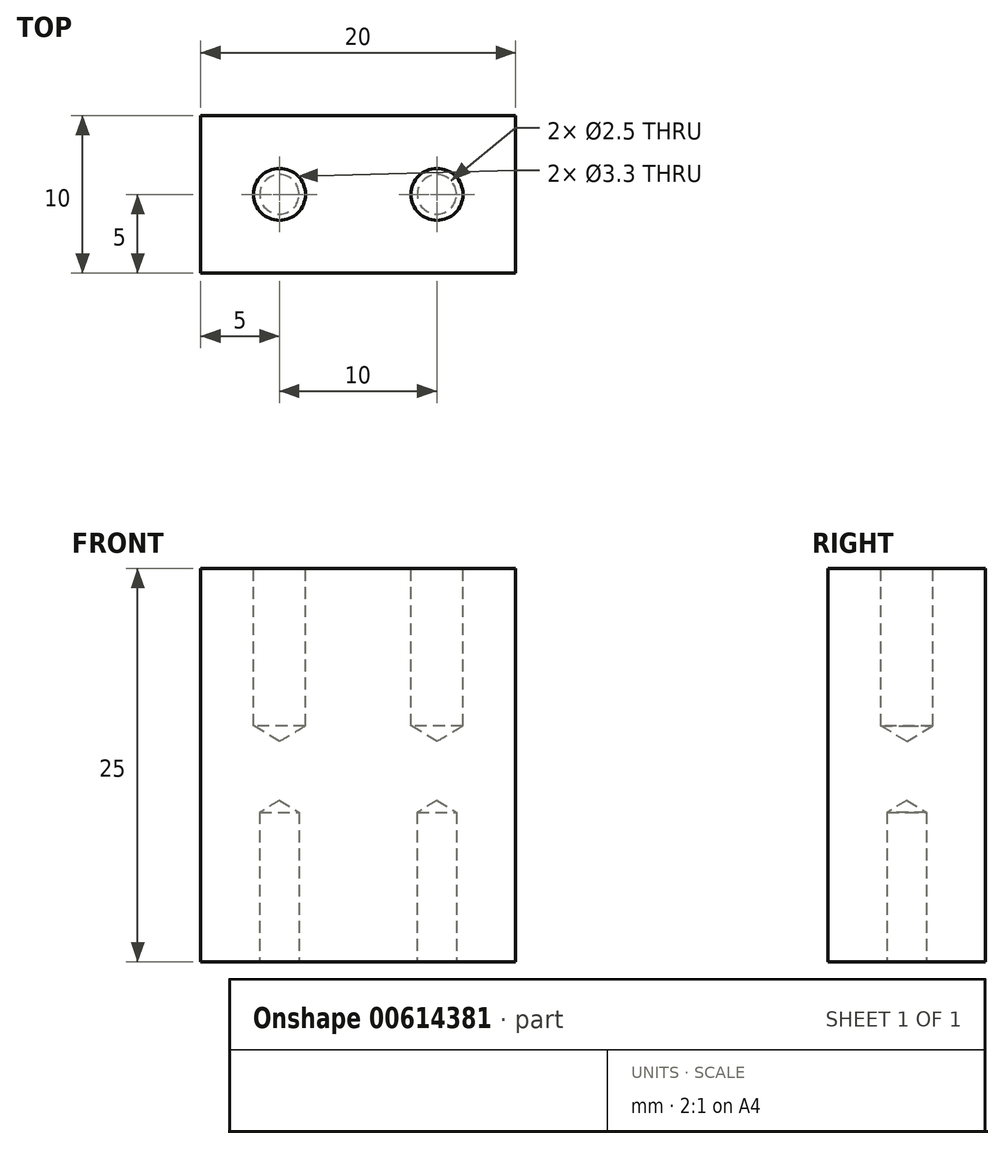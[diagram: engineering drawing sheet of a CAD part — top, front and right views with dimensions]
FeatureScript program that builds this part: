
annotation { "Feature Type Name" : "Feature", "Feature Type Description" : "" }
export const myFeature = defineFeature(function(context is Context, id is Id, definition is map)
    precondition{}
    {
        {
            var Q0;
            Q0=qCreatedBy(makeId("Top.planeOp"),FACE);
            var sketch = newSketch(context, id + "F0", { "sketchPlane" : qUnion([Q0])});
            skLineSegment(sketch, "E0.bottom", {"start": v(-10, 5) * mm, "end": v(10, 5) * mm});
            skLineSegment(sketch, "E0.top", {"start": v(-10, -5) * mm, "end": v(10, -5) * mm});
            skLineSegment(sketch, "E0.left", {"start": v(-10, 5) * mm, "end": v(-10, -5) * mm});
            skLineSegment(sketch, "E0.right", {"start": v(10, 5) * mm, "end": v(10, -5) * mm});
            skLineSegment(sketch, "E1", {"start": v(-10, 5) * mm, "end": v(10, -5) * mm, "construction": true});
            skLineSegment(sketch, "E2", {"start": v(10, 5) * mm, "end": v(-10, -5) * mm, "construction": true});
            skPoint(sketch, "E3", {"position": v(0, 0) * mm});
            skPoint(sketch, "E4", {"position": v(-5, 0) * mm});
            skPoint(sketch, "E5", {"position": v(5, 0) * mm});
            skSolve(sketch);
        }
        {
            var Q0;
            Q0=makeQuery(id+"F0.imprint","IMPRINT",FACE,{"disambiguationData":[TD([[makeQuery(id+"F0.imprint","IMPRINT",EDGE,{"derivedFrom":sQuery(id+"F0.wireOp",EDGE,"E0.bottom")}),-1.0]])]});
            extrude(context, id + "F1", {"entities" : qUnion([Q0]), "oppositeDirection" : true, "depth" : 25 * mm, "offsetDistance" : 25 * mm});
        }
        {
            var Q0;
            Q0=makeQuery(id+"F1.opExtrude","CAP_FACE",FACE,{"disambiguationData":[OSD([sQuery(id+"F0.wireOp",EDGE,"E0.bottom"),sQuery(id+"F0.wireOp",EDGE,"E0.top"),sQuery(id+"F0.wireOp",EDGE,"E0.left"),sQuery(id+"F0.wireOp",EDGE,"E0.right")])],"isStart":false});
            var sketch = newSketch(context, id + "F2", { "sketchPlane" : qUnion([Q0])});
            skPoint(sketch, "E6.0", {"position": v(-5, 0) * mm});
            skPoint(sketch, "E7.0", {"position": v(5, 0) * mm});
            skSolve(sketch);
        }
        {
            var Q0;
            Q0=sQuery(id+"F2.wireOp",VERTEX,"E6.0");
            var Q1;
            Q1=sQuery(id+"F2.wireOp",VERTEX,"E7.0");
            var Q2;
            Q2=makeQuery(id+"F1.opExtrude","SWEPT_BODY",BODY,{"disambiguationData":[OSD([sQuery(id+"F0.wireOp",EDGE,"E0.bottom"),sQuery(id+"F0.wireOp",EDGE,"E0.top"),sQuery(id+"F0.wireOp",EDGE,"E0.left"),sQuery(id+"F0.wireOp",EDGE,"E0.right")])]});
            hole(context, id + "F3", {"style" : HoleStyle.SIMPLE, "endStyle" : HoleEndStyle.BLIND, "standardTappedOrClearance" : lookupTablePath({ "standard" : "ISO", "engagement" : "75%", "pitch" : "0.5 mm", "size" : "M3", "type" : "Tapped" }), "standardBlindInLast" : lookupTablePath({ "standard" : "ISO", "engagement" : "75%", "pitch" : "0.5 mm", "size" : "M3", "type" : "Tapped" }), "holeDiameter" : 2.5 * mm, "majorDiameter" : 3 * mm, "showTappedDepth" : true, "holeDepth" : 9.5 * mm, "isTappedThrough" : true, "tappedDepth" : 8 * mm, "tapClearance" : 3, "locations" : qUnion([Q0, Q1]), "scope" : qUnion([Q2])});
        }
        {
            var Q0;
            Q0=sQuery(id+"F0.wireOp",VERTEX,"E4");
            var Q1;
            Q1=sQuery(id+"F0.wireOp",VERTEX,"E5");
            var Q2;
            Q2=makeQuery(id+"F1.opExtrude","SWEPT_BODY",BODY,{"disambiguationData":[OSD([sQuery(id+"F0.wireOp",EDGE,"E0.bottom"),sQuery(id+"F0.wireOp",EDGE,"E0.top"),sQuery(id+"F0.wireOp",EDGE,"E0.left"),sQuery(id+"F0.wireOp",EDGE,"E0.right")])]});
            hole(context, id + "F4", {"style" : HoleStyle.SIMPLE, "endStyle" : HoleEndStyle.BLIND, "standardTappedOrClearance" : lookupTablePath({ "standard" : "ISO", "engagement" : "75%", "pitch" : "0.7 mm", "size" : "M4", "type" : "Tapped" }), "standardBlindInLast" : lookupTablePath({ "standard" : "ISO", "engagement" : "75%", "pitch" : "0.7 mm", "size" : "M4", "type" : "Tapped" }), "holeDiameter" : 3.3 * mm, "majorDiameter" : 4 * mm, "showTappedDepth" : true, "holeDepth" : 10 * mm, "isTappedThrough" : true, "tappedDepth" : 7.9 * mm, "tapClearance" : 3, "locations" : qUnion([Q0, Q1]), "scope" : qUnion([Q2])});
        }
    });
